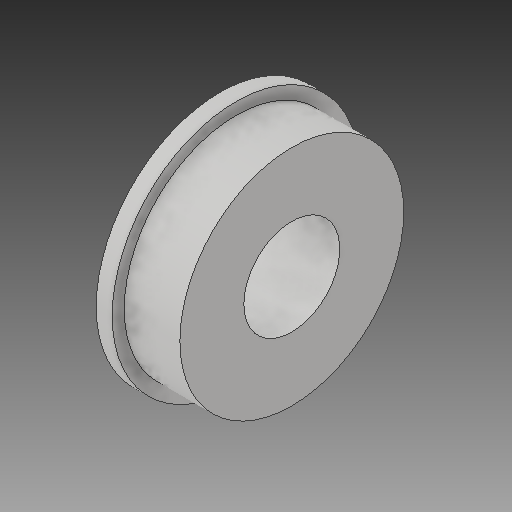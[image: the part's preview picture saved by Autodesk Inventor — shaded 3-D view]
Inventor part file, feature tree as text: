
AUTODESK INVENTOR PART (.ipt)
format: ipt  version: 2017 (Build 210142000, 142)  size: 123,392 bytes
history: native  units: in
note: dims shown in document units (in); Inventor stores cm internally (conversion verified against a paired STEP export)
features: revolve x1
ambient origin geometry x8: Origin, YZ Plane, XZ Plane, XY Plane, X Axis, Y Axis, Z Axis, Center Point
bodies: Solid1 (feature_tree)
feature tree (1):
  revolve  "Revolve1"  [1 undecoded]
note: 1 required parameter value undecoded (feature->parameter linkage not recoverable at this tier; creation-order binding heuristic only, values carry confidence <= 0.55)
